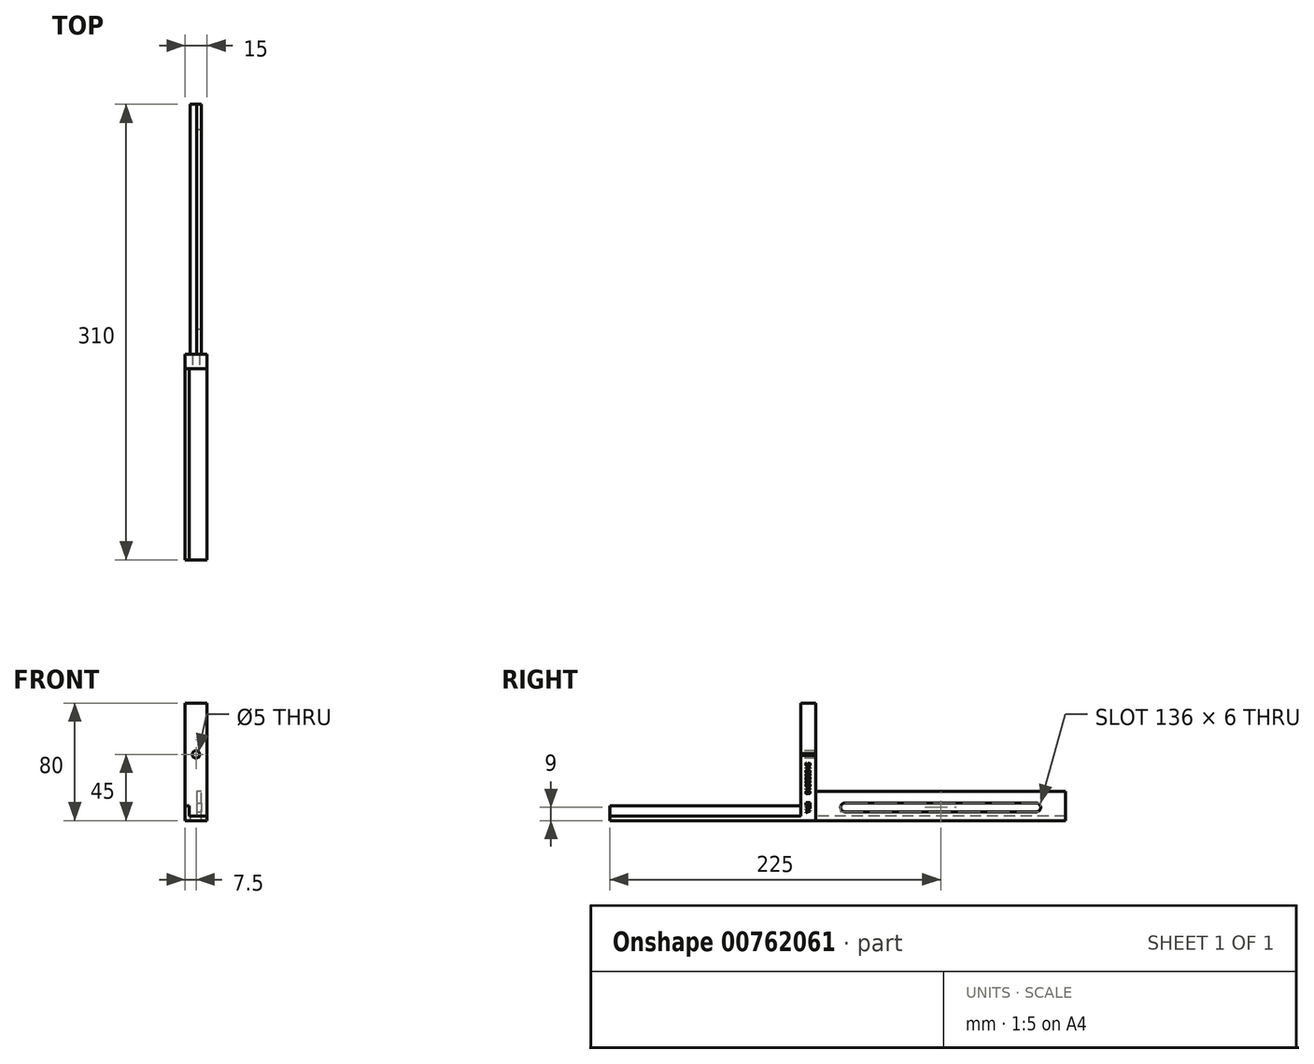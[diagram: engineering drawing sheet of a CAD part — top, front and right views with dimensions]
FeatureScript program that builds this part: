
annotation { "Feature Type Name" : "Feature", "Feature Type Description" : "" }
export const myFeature = defineFeature(function(context is Context, id is Id, definition is map)
    precondition{}
    {
        {
            var Q0;
            Q0=qCreatedBy(makeId("Top.planeOp"),FACE);
            var sketch = newSketch(context, id + "F0", { "sketchPlane" : qUnion([Q0])});
            skLineSegment(sketch, "E0.bottom", {"start": v(7.5, 5) * mm, "end": v(-7.5, 5) * mm});
            skLineSegment(sketch, "E0.top", {"start": v(7.5, -5) * mm, "end": v(-7.5, -5) * mm});
            skLineSegment(sketch, "E0.left", {"start": v(7.5, 5) * mm, "end": v(7.5, -5) * mm});
            skLineSegment(sketch, "E0.right", {"start": v(-7.5, 5) * mm, "end": v(-7.5, -5) * mm});
            skPoint(sketch, "E0.middle", {"position": v(0, 0) * mm});
            skSolve(sketch);
        }
        {
            var Q0;
            Q0 = qSketchRegion(id + "F0", true);
            extrude(context, id + "F1", {"entities" : qUnion([Q0]), "depth" : 80 * mm, "offsetDistance" : 25 * mm});
        }
        {
            var Q0;
            Q0=makeQuery(id+"F1.opExtrude","SWEPT_FACE",FACE,{"disambiguationData":[OSD([sQuery(id+"F0.wireOp",EDGE,"E0.top")])]});
            var sketch = newSketch(context, id + "F2", { "sketchPlane" : qUnion([Q0])});
            skLineSegment(sketch, "E1", {"start": v(7.5, 0) * mm, "end": v(-7.5, 0) * mm});
            skLineSegment(sketch, "E2", {"start": v(-7.5, 0) * mm, "end": v(-7.5, 10) * mm});
            skLineSegment(sketch, "E3", {"start": v(-7.5, 10) * mm, "end": v(-4.5, 10) * mm});
            skLineSegment(sketch, "E4", {"start": v(-4.5, 10) * mm, "end": v(-4.5, 3) * mm});
            skLineSegment(sketch, "E5", {"start": v(-4.5, 3) * mm, "end": v(7.5, 3) * mm});
            skLineSegment(sketch, "E6", {"start": v(7.5, 3) * mm, "end": v(7.5, 0) * mm});
            skSolve(sketch);
        }
        {
            var Q0;
            Q0=makeQuery(id+"F2.imprint","IMPRINT",FACE,{"disambiguationData":[TD([[makeQuery(id+"F2.imprint","IMPRINT",EDGE,{"derivedFrom":sQuery(id+"F2.wireOp",EDGE,"E1")}),-1.0]])]});
            extrude(context, id + "F3", {"entities" : qUnion([Q0]), "operationType" : NewBodyOperationType.ADD, "depth" : 130 * mm, "offsetDistance" : 25 * mm});
        }
        {
            var Q0;
            Q0=makeQuery(id+"F1.opExtrude","SWEPT_FACE",FACE,{"disambiguationData":[OSD([sQuery(id+"F0.wireOp",EDGE,"E0.bottom")])]});
            var sketch = newSketch(context, id + "F4", { "sketchPlane" : qUnion([Q0])});
            skLineSegment(sketch, "E7", {"start": v(4, 0) * mm, "end": v(-3.5, 0) * mm});
            skLineSegment(sketch, "E8", {"start": v(-3.5, 0) * mm, "end": v(-3.5, 20) * mm});
            skLineSegment(sketch, "E9", {"start": v(-3.5, 20) * mm, "end": v(-0.5, 20) * mm});
            skLineSegment(sketch, "E10", {"start": v(-0.5, 20) * mm, "end": v(-0.5, 3) * mm});
            skLineSegment(sketch, "E11", {"start": v(-0.5, 3) * mm, "end": v(4, 3) * mm});
            skLineSegment(sketch, "E12", {"start": v(4, 3) * mm, "end": v(4, 0) * mm});
            skSolve(sketch);
        }
        {
            var Q0;
            Q0=makeQuery(id+"F4.imprint","IMPRINT",FACE,{"disambiguationData":[TD([[makeQuery(id+"F4.imprint","IMPRINT",EDGE,{"derivedFrom":sQuery(id+"F4.wireOp",EDGE,"E7")}),1.0]])]});
            extrude(context, id + "F5", {"entities" : qUnion([Q0]), "operationType" : NewBodyOperationType.ADD, "depth" : 170 * mm, "offsetDistance" : 25 * mm});
        }
        {
            var Q0;
            Q0=makeQuery(id+"F5.opExtrude","SWEPT_FACE",FACE,{"disambiguationData":[OSD([sQuery(id+"F4.wireOp",EDGE,"E8")])]});
            var sketch = newSketch(context, id + "F6", { "sketchPlane" : qUnion([Q0])});
            skLineSegment(sketch, "E13", {"start": v(25, 12) * mm, "end": v(155, 12) * mm});
            skLineSegment(sketch, "E14", {"start": v(25, 6) * mm, "end": v(155, 6) * mm});
            skLineSegment(sketch, "E15", {"start": v(25, 9) * mm, "end": v(155, 9) * mm, "construction": true});
            skLineSegment(sketch, "E16", {"start": v(25, 6) * mm, "end": v(25, 12) * mm, "construction": true});
            skLineSegment(sketch, "E17", {"start": v(155, 6) * mm, "end": v(155, 12) * mm, "construction": true});
            skArc(sketch, "E18", {"start": v(25, 6) * mm, "mid": v(22, 9) * mm, "end": v(25, 12) * mm});
            skArc(sketch, "E19", {"start": v(155, 6) * mm, "mid": v(158, 9) * mm, "end": v(155, 12) * mm});
            skSolve(sketch);
        }
        {
            var Q0;
            Q0=makeQuery(id+"F6.imprint","IMPRINT",FACE,{"disambiguationData":[TD([[makeQuery(id+"F6.imprint","IMPRINT",EDGE,{"derivedFrom":sQuery(id+"F6.wireOp",EDGE,"E13")}),-1.0]])]});
            extrude(context, id + "F7", {"entities" : qUnion([Q0]), "operationType" : NewBodyOperationType.REMOVE, "oppositeDirection" : true, "depth" : 5 * mm, "offsetDistance" : 25 * mm});
        }
        {
            var Q0;
            Q0=makeQuery(id+"F1.opExtrude","SWEPT_FACE",FACE,{"disambiguationData":[OSD([sQuery(id+"F0.wireOp",EDGE,"E0.top")])]});
            var sketch = newSketch(context, id + "F8", { "sketchPlane" : qUnion([Q0])});
            skLineSegment(sketch, "E20", {"start": v(0, 80) * mm, "end": v(0, 0) * mm, "construction": true});
            skPoint(sketch, "E21", {"position": v(0, 45) * mm});
            skSolve(sketch);
        }
        {
            var Q0;
            Q0=sQuery(id+"F8.wireOp",VERTEX,"E21");
            var Q1;
            Q1=makeQuery(id+"F1.opExtrude","SWEPT_BODY",BODY,{"disambiguationData":[OSD([sQuery(id+"F0.wireOp",EDGE,"E0.bottom"),sQuery(id+"F0.wireOp",EDGE,"E0.top"),sQuery(id+"F0.wireOp",EDGE,"E0.left"),sQuery(id+"F0.wireOp",EDGE,"E0.right")])]});
            hole(context, id + "F9", {"style" : HoleStyle.SIMPLE, "endStyle" : HoleEndStyle.THROUGH, "standardTappedOrClearance" : lookupTablePath({ "standard" : "ISO", "engagement" : "75%", "pitch" : "1 mm", "size" : "M6", "type" : "Tapped" }), "standardBlindInLast" : lookupTablePath({ "standard" : "ISO", "engagement" : "75%", "pitch" : "1 mm", "size" : "M6", "type" : "Tapped" }), "holeDiameter" : 5 * mm, "majorDiameter" : 6 * mm, "showTappedDepth" : true, "isTappedThrough" : true, "tappedDepth" : 12 * mm, "tapClearance" : 3, "startFromSketch" : true, "locations" : qUnion([Q0]), "scope" : qUnion([Q1])});
        }
        {
            var Q0;
            Q0=makeQuery(id+"F3.boolean.opBoolean","MERGE",FACE,{"derivedFrom":[makeQuery(id+"F1.opExtrude","SWEPT_FACE",FACE,{"disambiguationData":[OSD([sQuery(id+"F0.wireOp",EDGE,"E0.left")])]}),makeQuery(id+"F3.opExtrude","SWEPT_FACE",FACE,{"disambiguationData":[OSD([sQuery(id+"F2.wireOp",EDGE,"E6")])]})]});
            var sketch = newSketch(context, id + "F10", { "sketchPlane" : qUnion([Q0])});
            skText(sketch, "E22", { "text": "316080018     E7A", "fontName": "OpenSans-Regular.ttf"});
            const initialGuessF10  = {"E22": [-0.00173, 0.03946, 0, -1, 0.003]};
            skSetInitialGuess(sketch, initialGuessF10);
            skSolve(sketch);
        }
        {
            var Q0;
            Q0 = qSketchRegion(id + "F10", true);
            extrude(context, id + "F11", {"entities" : qUnion([Q0]), "operationType" : NewBodyOperationType.REMOVE, "oppositeDirection" : true, "depth" : 0.2 * mm, "offsetDistance" : 25 * mm});
        }
        {
            var Q0;
            Q0=makeQuery(id+"F1.opExtrude","SWEPT_FACE",FACE,{"disambiguationData":[OSD([sQuery(id+"F0.wireOp",EDGE,"E0.bottom")])]});
            var sketch = newSketch(context, id + "F12", { "sketchPlane" : qUnion([Q0])});
            skLineSegment(sketch, "E23", {"start": v(-7.5, 45.5) * mm, "end": v(-7, 45) * mm});
            skLineSegment(sketch, "E24", {"start": v(-7, 45) * mm, "end": v(-7.5, 44.5) * mm});
            skLineSegment(sketch, "E25", {"start": v(-7.5, 45.5) * mm, "end": v(-7.5, 44.5) * mm});
            skSolve(sketch);
        }
        {
            var Q0;
            Q0 = qSketchRegion(id + "F12", true);
            extrude(context, id + "F13", {"entities" : qUnion([Q0]), "operationType" : NewBodyOperationType.REMOVE, "oppositeDirection" : true, "depth" : 15 * mm, "offsetDistance" : 25 * mm});
        }
    });
